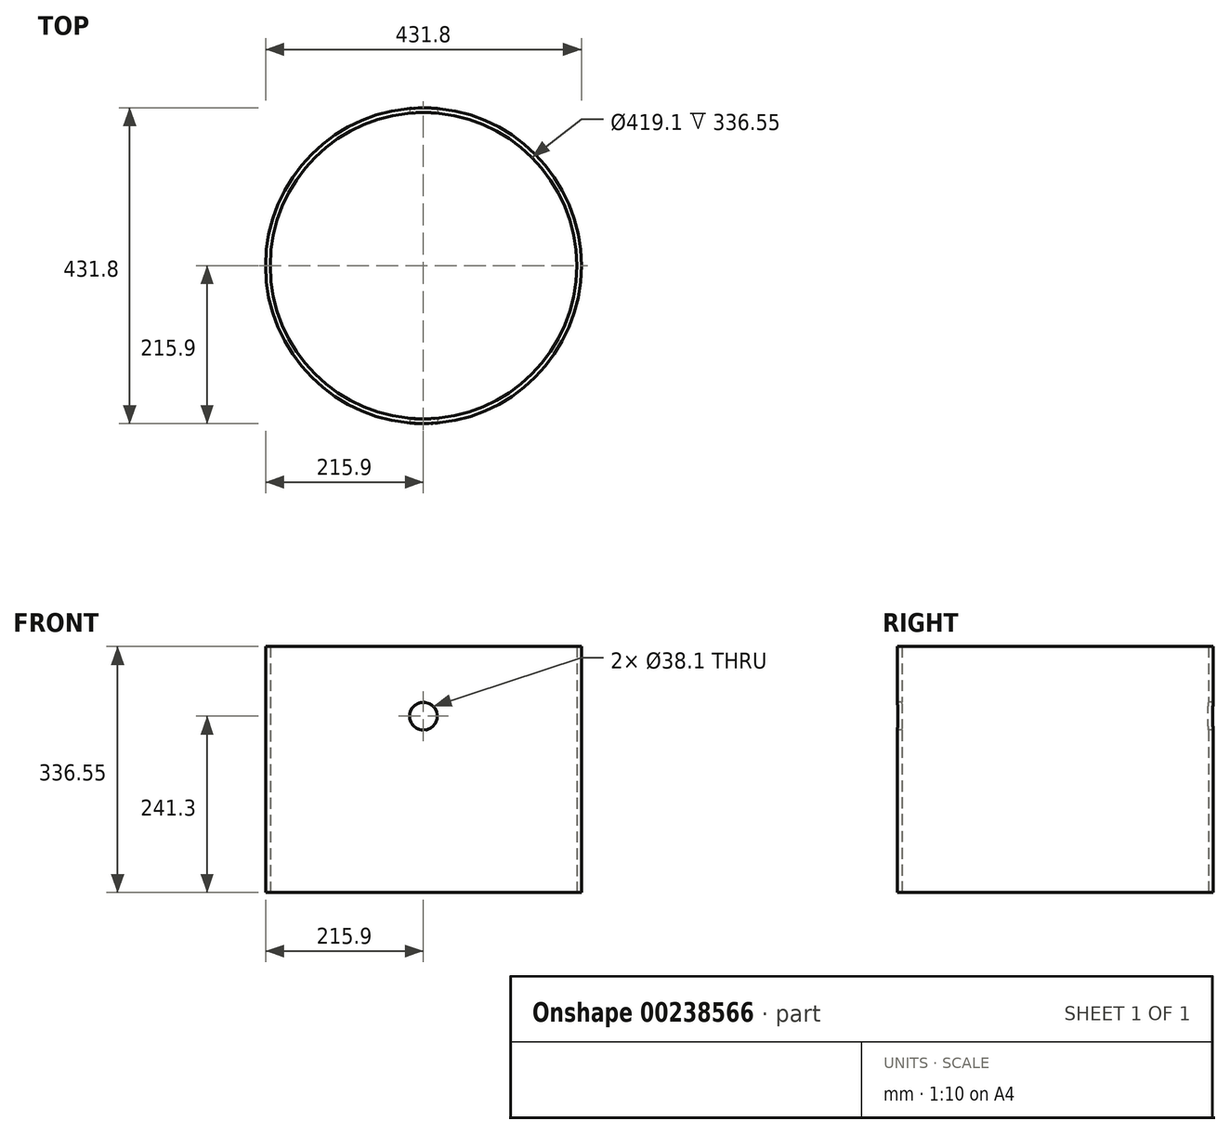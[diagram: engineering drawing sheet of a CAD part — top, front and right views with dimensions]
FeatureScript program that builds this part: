
annotation { "Feature Type Name" : "Feature", "Feature Type Description" : "" }
export const myFeature = defineFeature(function(context is Context, id is Id, definition is map)
    precondition{}
    {
        {
            var Q0;
            Q0=qCreatedBy(makeId("Top.planeOp"),FACE);
            var sketch = newSketch(context, id + "F0", { "sketchPlane" : qUnion([Q0])});
            skCircle(sketch, "E0", {"center": v(0, 0) * mm, "radius": 215.9 * mm});
            skSolve(sketch);
        }
        {
            var Q0;
            Q0=makeQuery(id+"F0.imprint","IMPRINT",FACE,{"disambiguationData":[TD([[makeQuery(id+"F0.imprint","IMPRINT",EDGE,{"derivedFrom":sQuery(id+"F0.wireOp",EDGE,"E0")}),1.0]])]});
            extrude(context, id + "F1", {"entities" : qUnion([Q0]), "depth" : 336.55 * mm});
        }
        {
            var Q0;
            Q0=makeQuery(id+"F1.opExtrude","CAP_FACE",FACE,{"disambiguationData":[OSD([sQuery(id+"F0.wireOp",EDGE,"E0")])],"isStart":false});
            var Q1;
            Q1=makeQuery(id+"F1.opExtrude","CAP_FACE",FACE,{"disambiguationData":[OSD([sQuery(id+"F0.wireOp",EDGE,"E0")])],"isStart":true});
            shell(context, id + "F2", {"entities" : qUnion([Q0, Q1]), "thickness" : 6.35 * mm});
        }
        {
            var Q0;
            Q0=qCreatedBy(makeId("Front.planeOp"),FACE);
            var sketch = newSketch(context, id + "F3", { "sketchPlane" : qUnion([Q0])});
            skCircle(sketch, "E1", {"center": v(0, 241.3) * mm, "radius": 19.05 * mm});
            skSolve(sketch);
        }
        {
            var Q0;
            Q0=makeQuery(id+"F3.imprint","IMPRINT",FACE,{"disambiguationData":[TD([[makeQuery(id+"F3.imprint","IMPRINT",EDGE,{"derivedFrom":sQuery(id+"F3.wireOp",EDGE,"E1")}),1.0]])]});
            extrude(context, id + "F4", {"entities" : qUnion([Q0]), "operationType" : NewBodyOperationType.REMOVE, "oppositeDirection" : true, "depth" : 508 * mm, "symmetric" : true});
        }
    });
